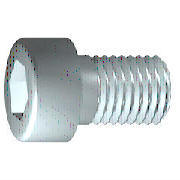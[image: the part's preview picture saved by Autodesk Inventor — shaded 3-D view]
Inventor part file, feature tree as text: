
AUTODESK INVENTOR PART (.ipt)
format: ipt  version: 2020 (Build 240168000, 168)  size: 188,416 bytes
history: native  units: mm (DEFAULTED — no unit token found)
features: sketch x2, other x1, extrude x1, plane x1, fillet x1
ambient origin geometry x7: Origin, YZ Plane, XY Plane, X Axis, Y Axis, Z Axis, Center Point
bodies: Solid1 (feature_tree)
feature tree (6):
  other  "Körper"
  extrude  "Loch"  Depth=3.0mm
  plane  "Work Plane1"
  fillet  "Fillet2"  Radius=3.0mm
  sketch  "Skizze1"  dims[d1=18.0mm d2=0.306825mm d3=3.0mm]
  sketch  "Skizze2"  dims[d4=1.3mm d5=60.0deg d6=3.0mm d7=3.0mm d8=2.886751mm d9=5.5mm d10=90.0deg d11=10.0mm d12=0.0mm d13=18.0mm d14=0.0mm d15=0.306725mm d16=0.306725mm d17=0.3mm d19=0.0mm d26=30.0mm d27=45.0deg d28=0.0mm d29=0.0mm d30=0.1mm]
